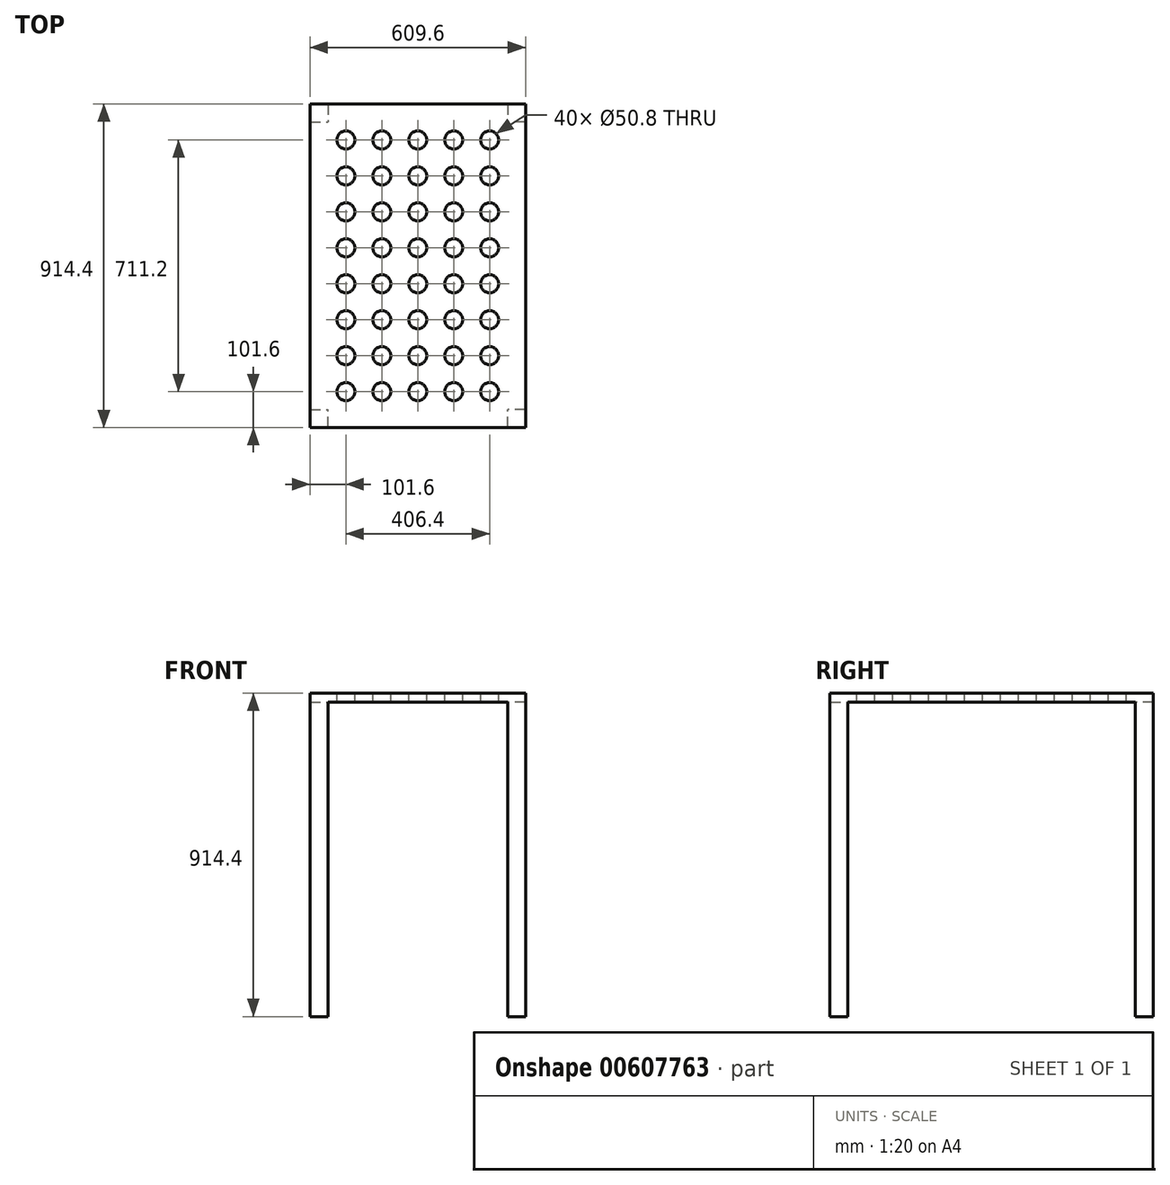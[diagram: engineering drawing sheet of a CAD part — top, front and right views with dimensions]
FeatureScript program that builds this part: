
annotation { "Feature Type Name" : "Feature", "Feature Type Description" : "" }
export const myFeature = defineFeature(function(context is Context, id is Id, definition is map)
    precondition{}
    {
        {
            var Q0;
            Q0=qCreatedBy(makeId("Top.planeOp"),FACE);
            var sketch = newSketch(context, id + "F0", { "sketchPlane" : qUnion([Q0])});
            skLineSegment(sketch, "E0.bottom", {"start": v(0, 0) * mm, "end": v(609.6, 0) * mm});
            skLineSegment(sketch, "E0.top", {"start": v(0, -914.4) * mm, "end": v(609.6, -914.4) * mm});
            skLineSegment(sketch, "E0.left", {"start": v(0, 0) * mm, "end": v(0, -914.4) * mm});
            skLineSegment(sketch, "E0.right", {"start": v(609.6, 0) * mm, "end": v(609.6, -914.4) * mm});
            skSolve(sketch);
        }
        {
            var Q0;
            Q0=makeQuery(id+"F0.imprint","IMPRINT",FACE,{"disambiguationData":[TD([[makeQuery(id+"F0.imprint","IMPRINT",EDGE,{"derivedFrom":sQuery(id+"F0.wireOp",EDGE,"E0.bottom")}),-1.0]])]});
            extrude(context, id + "F1", {"entities" : qUnion([Q0]), "oppositeDirection" : true, "depth" : 914.4 * mm, "offsetDistance" : 25.4 * mm});
        }
        {
            var Q0;
            Q0=makeQuery(id+"F1.opExtrude","CAP_FACE",FACE,{"disambiguationData":[OSD([sQuery(id+"F0.wireOp",EDGE,"E0.bottom"),sQuery(id+"F0.wireOp",EDGE,"E0.top"),sQuery(id+"F0.wireOp",EDGE,"E0.left"),sQuery(id+"F0.wireOp",EDGE,"E0.right")])],"isStart":false});
            var sketch = newSketch(context, id + "F2", { "sketchPlane" : qUnion([Q0])});
            skLineSegment(sketch, "E1.bottom", {"start": v(0, 0) * mm, "end": v(50.8, 0) * mm});
            skLineSegment(sketch, "E1.top", {"start": v(0, 50.8) * mm, "end": v(50.8, 50.8) * mm});
            skLineSegment(sketch, "E1.left", {"start": v(0, 0) * mm, "end": v(0, 50.8) * mm});
            skLineSegment(sketch, "E1.right", {"start": v(50.8, 0) * mm, "end": v(50.8, 50.8) * mm});
            skLineSegment(sketch, "E2.bottom", {"start": v(609.6, 0) * mm, "end": v(558.8, 0) * mm});
            skLineSegment(sketch, "E2.top", {"start": v(609.6, 50.8) * mm, "end": v(558.8, 50.8) * mm});
            skLineSegment(sketch, "E2.left", {"start": v(609.6, 0) * mm, "end": v(609.6, 50.8) * mm});
            skLineSegment(sketch, "E2.right", {"start": v(558.8, 0) * mm, "end": v(558.8, 50.8) * mm});
            skLineSegment(sketch, "E3.bottom", {"start": v(609.6, 914.4) * mm, "end": v(558.8, 914.4) * mm});
            skLineSegment(sketch, "E3.top", {"start": v(609.6, 863.6) * mm, "end": v(558.8, 863.6) * mm});
            skLineSegment(sketch, "E3.left", {"start": v(609.6, 914.4) * mm, "end": v(609.6, 863.6) * mm});
            skLineSegment(sketch, "E3.right", {"start": v(558.8, 914.4) * mm, "end": v(558.8, 863.6) * mm});
            skLineSegment(sketch, "E4.bottom", {"start": v(0, 914.4) * mm, "end": v(50.8, 914.4) * mm});
            skLineSegment(sketch, "E4.top", {"start": v(0, 863.6) * mm, "end": v(50.8, 863.6) * mm});
            skLineSegment(sketch, "E4.left", {"start": v(0, 914.4) * mm, "end": v(0, 863.6) * mm});
            skLineSegment(sketch, "E4.right", {"start": v(50.8, 914.4) * mm, "end": v(50.8, 863.6) * mm});
            skSolve(sketch);
        }
        {
            var Q0;
            {var subQ5=sQuery(id+"F2.wireOp",EDGE,"E1.top");Q0=makeQuery(id+"F2.imprint","IMPRINT",FACE,{"disambiguationData":[TD([[makeQuery(id+"F2.imprint","IMPRINT",EDGE,{"derivedFrom":subQ5}),1.0]])]});}
            extrude(context, id + "F3", {"entities" : qUnion([Q0]), "operationType" : NewBodyOperationType.REMOVE, "oppositeDirection" : true, "depth" : 889 * mm, "offsetDistance" : 25.4 * mm});
        }
        {
            var Q0;
            Q0=makeQuery(id+"F1.opExtrude","CAP_FACE",FACE,{"disambiguationData":[OSD([sQuery(id+"F0.wireOp",EDGE,"E0.bottom"),sQuery(id+"F0.wireOp",EDGE,"E0.top"),sQuery(id+"F0.wireOp",EDGE,"E0.left"),sQuery(id+"F0.wireOp",EDGE,"E0.right")])],"isStart":true});
            var sketch = newSketch(context, id + "F4", { "sketchPlane" : qUnion([Q0])});
            skCircle(sketch, "E5", {"center": v(101.6, -101.6) * mm, "radius": 25.4 * mm});
            skCircle(sketch, "E6.0.1.0", {"center": v(101.6, -203.2) * mm, "radius": 25.4 * mm});
            skCircle(sketch, "E6.0.2.0", {"center": v(101.6, -304.8) * mm, "radius": 25.4 * mm});
            skCircle(sketch, "E6.0.3.0", {"center": v(101.6, -406.4) * mm, "radius": 25.4 * mm});
            skCircle(sketch, "E6.0.4.0", {"center": v(101.6, -508) * mm, "radius": 25.4 * mm});
            skCircle(sketch, "E6.0.5.0", {"center": v(101.6, -609.6) * mm, "radius": 25.4 * mm});
            skCircle(sketch, "E6.0.6.0", {"center": v(101.6, -711.2) * mm, "radius": 25.4 * mm});
            skCircle(sketch, "E6.0.7.0", {"center": v(101.6, -812.8) * mm, "radius": 25.4 * mm});
            skCircle(sketch, "E6.1.0.0", {"center": v(203.2, -101.6) * mm, "radius": 25.4 * mm});
            skCircle(sketch, "E6.1.1.0", {"center": v(203.2, -203.2) * mm, "radius": 25.4 * mm});
            skCircle(sketch, "E6.1.2.0", {"center": v(203.2, -304.8) * mm, "radius": 25.4 * mm});
            skCircle(sketch, "E6.1.3.0", {"center": v(203.2, -406.4) * mm, "radius": 25.4 * mm});
            skCircle(sketch, "E6.1.4.0", {"center": v(203.2, -508) * mm, "radius": 25.4 * mm});
            skCircle(sketch, "E6.1.5.0", {"center": v(203.2, -609.6) * mm, "radius": 25.4 * mm});
            skCircle(sketch, "E6.1.6.0", {"center": v(203.2, -711.2) * mm, "radius": 25.4 * mm});
            skCircle(sketch, "E6.1.7.0", {"center": v(203.2, -812.8) * mm, "radius": 25.4 * mm});
            skCircle(sketch, "E6.2.0.0", {"center": v(304.8, -101.6) * mm, "radius": 25.4 * mm});
            skCircle(sketch, "E6.2.1.0", {"center": v(304.8, -203.2) * mm, "radius": 25.4 * mm});
            skCircle(sketch, "E6.2.2.0", {"center": v(304.8, -304.8) * mm, "radius": 25.4 * mm});
            skCircle(sketch, "E6.2.3.0", {"center": v(304.8, -406.4) * mm, "radius": 25.4 * mm});
            skCircle(sketch, "E6.2.4.0", {"center": v(304.8, -508) * mm, "radius": 25.4 * mm});
            skCircle(sketch, "E6.2.5.0", {"center": v(304.8, -609.6) * mm, "radius": 25.4 * mm});
            skCircle(sketch, "E6.2.6.0", {"center": v(304.8, -711.2) * mm, "radius": 25.4 * mm});
            skCircle(sketch, "E6.2.7.0", {"center": v(304.8, -812.8) * mm, "radius": 25.4 * mm});
            skCircle(sketch, "E6.3.0.0", {"center": v(406.4, -101.6) * mm, "radius": 25.4 * mm});
            skCircle(sketch, "E6.3.1.0", {"center": v(406.4, -203.2) * mm, "radius": 25.4 * mm});
            skCircle(sketch, "E6.3.2.0", {"center": v(406.4, -304.8) * mm, "radius": 25.4 * mm});
            skCircle(sketch, "E6.3.3.0", {"center": v(406.4, -406.4) * mm, "radius": 25.4 * mm});
            skCircle(sketch, "E6.3.4.0", {"center": v(406.4, -508) * mm, "radius": 25.4 * mm});
            skCircle(sketch, "E6.3.5.0", {"center": v(406.4, -609.6) * mm, "radius": 25.4 * mm});
            skCircle(sketch, "E6.3.6.0", {"center": v(406.4, -711.2) * mm, "radius": 25.4 * mm});
            skCircle(sketch, "E6.3.7.0", {"center": v(406.4, -812.8) * mm, "radius": 25.4 * mm});
            skCircle(sketch, "E6.4.0.0", {"center": v(508, -101.6) * mm, "radius": 25.4 * mm});
            skCircle(sketch, "E6.4.1.0", {"center": v(508, -203.2) * mm, "radius": 25.4 * mm});
            skCircle(sketch, "E6.4.2.0", {"center": v(508, -304.8) * mm, "radius": 25.4 * mm});
            skCircle(sketch, "E6.4.3.0", {"center": v(508, -406.4) * mm, "radius": 25.4 * mm});
            skCircle(sketch, "E6.4.4.0", {"center": v(508, -508) * mm, "radius": 25.4 * mm});
            skCircle(sketch, "E6.4.5.0", {"center": v(508, -609.6) * mm, "radius": 25.4 * mm});
            skCircle(sketch, "E6.4.6.0", {"center": v(508, -711.2) * mm, "radius": 25.4 * mm});
            skCircle(sketch, "E6.4.7.0", {"center": v(508, -812.8) * mm, "radius": 25.4 * mm});
            skLineSegment(sketch, "E6.direction1", {"start": v(101.6, -101.6) * mm, "end": v(203.2, -101.6) * mm, "construction": true});
            skLineSegment(sketch, "E6.direction2", {"start": v(101.6, -101.6) * mm, "end": v(101.6, -203.2) * mm, "construction": true});
            skSolve(sketch);
        }
        {
            var Q0;
            Q0=makeQuery(id+"F4.imprint","IMPRINT",FACE,{"disambiguationData":[TD([[makeQuery(id+"F4.imprint","IMPRINT",EDGE,{"derivedFrom":sQuery(id+"F4.wireOp",EDGE,"E5")}),1.0]])]});
            var Q1;
            Q1=makeQuery(id+"F4.imprint","IMPRINT",FACE,{"disambiguationData":[TD([[makeQuery(id+"F4.imprint","IMPRINT",EDGE,{"derivedFrom":sQuery(id+"F4.wireOp",EDGE,"E6.1.0.0")}),1.0]])]});
            var Q2;
            Q2=makeQuery(id+"F4.imprint","IMPRINT",FACE,{"disambiguationData":[TD([[makeQuery(id+"F4.imprint","IMPRINT",EDGE,{"derivedFrom":sQuery(id+"F4.wireOp",EDGE,"E6.2.0.0")}),1.0]])]});
            var Q3;
            Q3=makeQuery(id+"F4.imprint","IMPRINT",FACE,{"disambiguationData":[TD([[makeQuery(id+"F4.imprint","IMPRINT",EDGE,{"derivedFrom":sQuery(id+"F4.wireOp",EDGE,"E6.3.0.0")}),1.0]])]});
            var Q4;
            Q4=makeQuery(id+"F4.imprint","IMPRINT",FACE,{"disambiguationData":[TD([[makeQuery(id+"F4.imprint","IMPRINT",EDGE,{"derivedFrom":sQuery(id+"F4.wireOp",EDGE,"E6.4.0.0")}),1.0]])]});
            var Q5;
            Q5=makeQuery(id+"F4.imprint","IMPRINT",FACE,{"disambiguationData":[TD([[makeQuery(id+"F4.imprint","IMPRINT",EDGE,{"derivedFrom":sQuery(id+"F4.wireOp",EDGE,"E6.4.1.0")}),1.0]])]});
            var Q6;
            Q6=makeQuery(id+"F4.imprint","IMPRINT",FACE,{"disambiguationData":[TD([[makeQuery(id+"F4.imprint","IMPRINT",EDGE,{"derivedFrom":sQuery(id+"F4.wireOp",EDGE,"E6.3.1.0")}),1.0]])]});
            var Q7;
            Q7=makeQuery(id+"F4.imprint","IMPRINT",FACE,{"disambiguationData":[TD([[makeQuery(id+"F4.imprint","IMPRINT",EDGE,{"derivedFrom":sQuery(id+"F4.wireOp",EDGE,"E6.2.1.0")}),1.0]])]});
            var Q8;
            Q8=makeQuery(id+"F4.imprint","IMPRINT",FACE,{"disambiguationData":[TD([[makeQuery(id+"F4.imprint","IMPRINT",EDGE,{"derivedFrom":sQuery(id+"F4.wireOp",EDGE,"E6.1.1.0")}),1.0]])]});
            var Q9;
            Q9=makeQuery(id+"F4.imprint","IMPRINT",FACE,{"disambiguationData":[TD([[makeQuery(id+"F4.imprint","IMPRINT",EDGE,{"derivedFrom":sQuery(id+"F4.wireOp",EDGE,"E6.0.1.0")}),1.0]])]});
            var Q10;
            Q10=makeQuery(id+"F4.imprint","IMPRINT",FACE,{"disambiguationData":[TD([[makeQuery(id+"F4.imprint","IMPRINT",EDGE,{"derivedFrom":sQuery(id+"F4.wireOp",EDGE,"E6.0.2.0")}),1.0]])]});
            var Q11;
            Q11=makeQuery(id+"F4.imprint","IMPRINT",FACE,{"disambiguationData":[TD([[makeQuery(id+"F4.imprint","IMPRINT",EDGE,{"derivedFrom":sQuery(id+"F4.wireOp",EDGE,"E6.1.2.0")}),1.0]])]});
            var Q12;
            Q12=makeQuery(id+"F4.imprint","IMPRINT",FACE,{"disambiguationData":[TD([[makeQuery(id+"F4.imprint","IMPRINT",EDGE,{"derivedFrom":sQuery(id+"F4.wireOp",EDGE,"E6.2.2.0")}),1.0]])]});
            var Q13;
            Q13=makeQuery(id+"F4.imprint","IMPRINT",FACE,{"disambiguationData":[TD([[makeQuery(id+"F4.imprint","IMPRINT",EDGE,{"derivedFrom":sQuery(id+"F4.wireOp",EDGE,"E6.3.2.0")}),1.0]])]});
            var Q14;
            Q14=makeQuery(id+"F4.imprint","IMPRINT",FACE,{"disambiguationData":[TD([[makeQuery(id+"F4.imprint","IMPRINT",EDGE,{"derivedFrom":sQuery(id+"F4.wireOp",EDGE,"E6.4.2.0")}),1.0]])]});
            var Q15;
            Q15=makeQuery(id+"F4.imprint","IMPRINT",FACE,{"disambiguationData":[TD([[makeQuery(id+"F4.imprint","IMPRINT",EDGE,{"derivedFrom":sQuery(id+"F4.wireOp",EDGE,"E6.4.3.0")}),1.0]])]});
            var Q16;
            Q16=makeQuery(id+"F4.imprint","IMPRINT",FACE,{"disambiguationData":[TD([[makeQuery(id+"F4.imprint","IMPRINT",EDGE,{"derivedFrom":sQuery(id+"F4.wireOp",EDGE,"E6.3.3.0")}),1.0]])]});
            var Q17;
            Q17=makeQuery(id+"F4.imprint","IMPRINT",FACE,{"disambiguationData":[TD([[makeQuery(id+"F4.imprint","IMPRINT",EDGE,{"derivedFrom":sQuery(id+"F4.wireOp",EDGE,"E6.2.3.0")}),1.0]])]});
            var Q18;
            Q18=makeQuery(id+"F4.imprint","IMPRINT",FACE,{"disambiguationData":[TD([[makeQuery(id+"F4.imprint","IMPRINT",EDGE,{"derivedFrom":sQuery(id+"F4.wireOp",EDGE,"E6.1.3.0")}),1.0]])]});
            var Q19;
            Q19=makeQuery(id+"F4.imprint","IMPRINT",FACE,{"disambiguationData":[TD([[makeQuery(id+"F4.imprint","IMPRINT",EDGE,{"derivedFrom":sQuery(id+"F4.wireOp",EDGE,"E6.0.3.0")}),1.0]])]});
            var Q20;
            Q20=makeQuery(id+"F4.imprint","IMPRINT",FACE,{"disambiguationData":[TD([[makeQuery(id+"F4.imprint","IMPRINT",EDGE,{"derivedFrom":sQuery(id+"F4.wireOp",EDGE,"E6.0.4.0")}),1.0]])]});
            var Q21;
            Q21=makeQuery(id+"F4.imprint","IMPRINT",FACE,{"disambiguationData":[TD([[makeQuery(id+"F4.imprint","IMPRINT",EDGE,{"derivedFrom":sQuery(id+"F4.wireOp",EDGE,"E6.1.4.0")}),1.0]])]});
            var Q22;
            Q22=makeQuery(id+"F4.imprint","IMPRINT",FACE,{"disambiguationData":[TD([[makeQuery(id+"F4.imprint","IMPRINT",EDGE,{"derivedFrom":sQuery(id+"F4.wireOp",EDGE,"E6.2.4.0")}),1.0]])]});
            var Q23;
            Q23=makeQuery(id+"F4.imprint","IMPRINT",FACE,{"disambiguationData":[TD([[makeQuery(id+"F4.imprint","IMPRINT",EDGE,{"derivedFrom":sQuery(id+"F4.wireOp",EDGE,"E6.3.4.0")}),1.0]])]});
            var Q24;
            Q24=makeQuery(id+"F4.imprint","IMPRINT",FACE,{"disambiguationData":[TD([[makeQuery(id+"F4.imprint","IMPRINT",EDGE,{"derivedFrom":sQuery(id+"F4.wireOp",EDGE,"E6.4.4.0")}),1.0]])]});
            var Q25;
            Q25=makeQuery(id+"F4.imprint","IMPRINT",FACE,{"disambiguationData":[TD([[makeQuery(id+"F4.imprint","IMPRINT",EDGE,{"derivedFrom":sQuery(id+"F4.wireOp",EDGE,"E6.4.5.0")}),1.0]])]});
            var Q26;
            Q26=makeQuery(id+"F4.imprint","IMPRINT",FACE,{"disambiguationData":[TD([[makeQuery(id+"F4.imprint","IMPRINT",EDGE,{"derivedFrom":sQuery(id+"F4.wireOp",EDGE,"E6.3.5.0")}),1.0]])]});
            var Q27;
            Q27=makeQuery(id+"F4.imprint","IMPRINT",FACE,{"disambiguationData":[TD([[makeQuery(id+"F4.imprint","IMPRINT",EDGE,{"derivedFrom":sQuery(id+"F4.wireOp",EDGE,"E6.2.5.0")}),1.0]])]});
            var Q28;
            Q28=makeQuery(id+"F4.imprint","IMPRINT",FACE,{"disambiguationData":[TD([[makeQuery(id+"F4.imprint","IMPRINT",EDGE,{"derivedFrom":sQuery(id+"F4.wireOp",EDGE,"E6.1.5.0")}),1.0]])]});
            var Q29;
            Q29=makeQuery(id+"F4.imprint","IMPRINT",FACE,{"disambiguationData":[TD([[makeQuery(id+"F4.imprint","IMPRINT",EDGE,{"derivedFrom":sQuery(id+"F4.wireOp",EDGE,"E6.0.5.0")}),1.0]])]});
            var Q30;
            Q30=makeQuery(id+"F4.imprint","IMPRINT",FACE,{"disambiguationData":[TD([[makeQuery(id+"F4.imprint","IMPRINT",EDGE,{"derivedFrom":sQuery(id+"F4.wireOp",EDGE,"E6.0.6.0")}),1.0]])]});
            var Q31;
            Q31=makeQuery(id+"F4.imprint","IMPRINT",FACE,{"disambiguationData":[TD([[makeQuery(id+"F4.imprint","IMPRINT",EDGE,{"derivedFrom":sQuery(id+"F4.wireOp",EDGE,"E6.1.6.0")}),1.0]])]});
            var Q32;
            Q32=makeQuery(id+"F4.imprint","IMPRINT",FACE,{"disambiguationData":[TD([[makeQuery(id+"F4.imprint","IMPRINT",EDGE,{"derivedFrom":sQuery(id+"F4.wireOp",EDGE,"E6.2.6.0")}),1.0]])]});
            var Q33;
            Q33=makeQuery(id+"F4.imprint","IMPRINT",FACE,{"disambiguationData":[TD([[makeQuery(id+"F4.imprint","IMPRINT",EDGE,{"derivedFrom":sQuery(id+"F4.wireOp",EDGE,"E6.3.6.0")}),1.0]])]});
            var Q34;
            Q34=makeQuery(id+"F4.imprint","IMPRINT",FACE,{"disambiguationData":[TD([[makeQuery(id+"F4.imprint","IMPRINT",EDGE,{"derivedFrom":sQuery(id+"F4.wireOp",EDGE,"E6.4.6.0")}),1.0]])]});
            var Q35;
            Q35=makeQuery(id+"F4.imprint","IMPRINT",FACE,{"disambiguationData":[TD([[makeQuery(id+"F4.imprint","IMPRINT",EDGE,{"derivedFrom":sQuery(id+"F4.wireOp",EDGE,"E6.4.7.0")}),1.0]])]});
            var Q36;
            Q36=makeQuery(id+"F4.imprint","IMPRINT",FACE,{"disambiguationData":[TD([[makeQuery(id+"F4.imprint","IMPRINT",EDGE,{"derivedFrom":sQuery(id+"F4.wireOp",EDGE,"E6.3.7.0")}),1.0]])]});
            var Q37;
            Q37=makeQuery(id+"F4.imprint","IMPRINT",FACE,{"disambiguationData":[TD([[makeQuery(id+"F4.imprint","IMPRINT",EDGE,{"derivedFrom":sQuery(id+"F4.wireOp",EDGE,"E6.2.7.0")}),1.0]])]});
            var Q38;
            Q38=makeQuery(id+"F4.imprint","IMPRINT",FACE,{"disambiguationData":[TD([[makeQuery(id+"F4.imprint","IMPRINT",EDGE,{"derivedFrom":sQuery(id+"F4.wireOp",EDGE,"E6.1.7.0")}),1.0]])]});
            var Q39;
            Q39=makeQuery(id+"F4.imprint","IMPRINT",FACE,{"disambiguationData":[TD([[makeQuery(id+"F4.imprint","IMPRINT",EDGE,{"derivedFrom":sQuery(id+"F4.wireOp",EDGE,"E6.0.7.0")}),1.0]])]});
            extrude(context, id + "F5", {"entities" : qUnion([Q0, Q1, Q2, Q3, Q4, Q5, Q6, Q7, Q8, Q9, Q10, Q11, Q12, Q13, Q14, Q15, Q16, Q17, Q18, Q19, Q20, Q21, Q22, Q23, Q24, Q25, Q26, Q27, Q28, Q29, Q30, Q31, Q32, Q33, Q34, Q35, Q36, Q37, Q38, Q39]), "operationType" : NewBodyOperationType.REMOVE, "endBound" : BoundingType.THROUGH_ALL, "oppositeDirection" : true, "depth" : 25.4 * mm, "offsetDistance" : 25.4 * mm});
        }
    });
